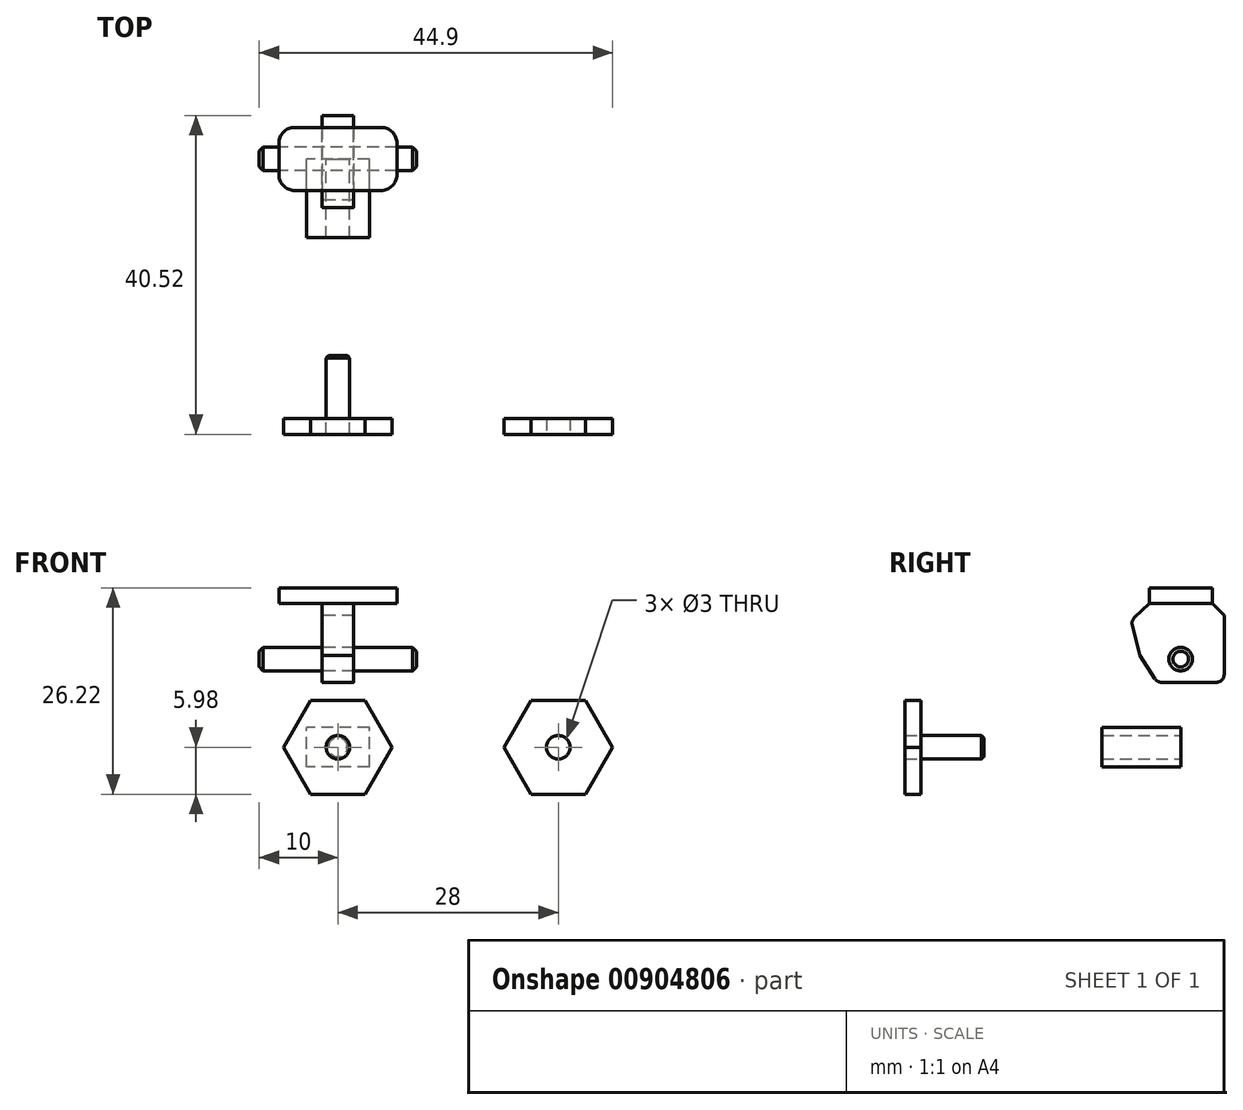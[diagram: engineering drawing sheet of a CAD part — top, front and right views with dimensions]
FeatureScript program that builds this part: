
annotation { "Feature Type Name" : "Feature", "Feature Type Description" : "" }
export const myFeature = defineFeature(function(context is Context, id is Id, definition is map)
    precondition{}
    {
        {
            var Q0;
            Q0=qCreatedBy(makeId("Front.planeOp"),FACE);
            var sketch = newSketch(context, id + "F0", { "sketchPlane" : qUnion([Q0])});
            skCircle(sketch, "E0", {"center": v(0, 0) * mm, "radius": 1.5 * mm});
            skLineSegment(sketch, "E1.bottom", {"start": v(4, -2.5) * mm, "end": v(-4, -2.5) * mm});
            skLineSegment(sketch, "E1.top", {"start": v(4, 2.5) * mm, "end": v(-4, 2.5) * mm});
            skLineSegment(sketch, "E1.left", {"start": v(4, -2.5) * mm, "end": v(4, 2.5) * mm});
            skLineSegment(sketch, "E1.right", {"start": v(-4, -2.5) * mm, "end": v(-4, 2.5) * mm});
            skSolve(sketch);
        }
        {
            var Q0;
            Q0 = qSketchRegion(id + "F0", true);
            extrude(context, id + "F1", {"entities" : qUnion([Q0]), "depth" : 10 * mm, "offsetDistance" : 25 * mm});
        }
        {
            var Q0;
            Q0=qCreatedBy(makeId("Front.planeOp"),FACE);
            cPlane(context, id + "F2", {"entities" : qUnion([Q0]), "cplaneType" : CPlaneType.OFFSET, "offset" : 25 * mm, "width" : 150 * mm, "height" : 150 * mm});
        }
        {
            var Q0;
            Q0=qCreatedBy(id+"F2.planeOp",FACE);
            var sketch = newSketch(context, id + "F3", { "sketchPlane" : qUnion([Q0])});
            skCircle(sketch, "E2", {"center": v(0, 0) * mm, "radius": 1.5 * mm});
            skSolve(sketch);
        }
        {
            var Q0;
            Q0 = qSketchRegion(id + "F3", true);
            extrude(context, id + "F4", {"entities" : qUnion([Q0]), "depth" : 10 * mm, "offsetDistance" : 25 * mm});
        }
        {
            var Q0;
            Q0=makeQuery(id+"F4.opExtrude","CAP_FACE",FACE,{"disambiguationData":[OSD([sQuery(id+"F3.wireOp",EDGE,"E2")])],"isStart":false});
            var sketch = newSketch(context, id + "F5", { "sketchPlane" : qUnion([Q0])});
            skLineSegment(sketch, "E3.0", {"start": v(6.9, 0) * mm, "end": v(3.45, -5.98) * mm});
            skLineSegment(sketch, "E3.1", {"start": v(3.45, -5.98) * mm, "end": v(-3.45, -5.98) * mm});
            skLineSegment(sketch, "E3.2", {"start": v(-3.45, -5.98) * mm, "end": v(-6.9, 0) * mm});
            skLineSegment(sketch, "E3.3", {"start": v(-6.9, 0) * mm, "end": v(-3.45, 5.98) * mm});
            skLineSegment(sketch, "E3.4", {"start": v(-3.45, 5.98) * mm, "end": v(3.45, 5.98) * mm});
            skLineSegment(sketch, "E3.5", {"start": v(3.45, 5.98) * mm, "end": v(6.9, 0) * mm});
            skPoint(sketch, "E3.0.midPoint", {"position": v(5.17, -2.99) * mm});
            skSolve(sketch);
        }
        {
            var Q0;
            Q0=makeQuery(id+"F5.imprint","IMPRINT",FACE,{"disambiguationData":[TD([[makeQuery(id+"F5.imprint","IMPRINT",EDGE,{"derivedFrom":sQuery(id+"F5.wireOp",EDGE,"E3.0")}),-1.0]])]});
            extrude(context, id + "F6", {"entities" : qUnion([Q0]), "oppositeDirection" : true, "depth" : 2 * mm, "offsetDistance" : 25 * mm});
        }
        {
            var Q0;
            Q0=makeQuery(id+"F4.opExtrude","CAP_EDGE",EDGE,{"disambiguationData":[OSD([sQuery(id+"F3.wireOp",EDGE,"E2")])],"isStart":true});
            var Q1;
            Q1=makeQuery(id+"F8.opPattern","COPY",EDGE,{"derivedFrom":makeQuery(id+"F4.opExtrude","CAP_EDGE",EDGE,{"disambiguationData":[OSD([sQuery(id+"F3.wireOp",EDGE,"E2")])],"isStart":true}),"instanceName":"1"});
            chamfer(context, id + "F7", {"entities" : qUnion([Q0, Q1]), "width" : 0.3 * mm, "tangentPropagation" : true});
        }
        {
            var Q0;
            Q0=makeQuery(id+"F6.opExtrude","SWEPT_BODY",BODY,{"disambiguationData":[OSD([sQuery(id+"F3.wireOp",EDGE,"E2"),sQuery(id+"F5.wireOp",EDGE,"E3.0"),sQuery(id+"F5.wireOp",EDGE,"E3.1"),sQuery(id+"F5.wireOp",EDGE,"E3.2"),sQuery(id+"F5.wireOp",EDGE,"E3.3"),sQuery(id+"F5.wireOp",EDGE,"E3.4"),sQuery(id+"F5.wireOp",EDGE,"E3.5")])]});
            transform(context, id + "F8", {"entities" : qUnion([Q0]), "transformType" : TransformType.TRANSLATION_3D, "dx" : 28 * mm, "dy" : 0 * mm, "dz" : 0 * mm, "makeCopy" : true});
        }
        {
            var Q0;
            Q0=qCreatedBy(makeId("Front.planeOp"),FACE);
            var sketch = newSketch(context, id + "F9", { "sketchPlane" : qUnion([Q0])});
            skLineSegment(sketch, "E4", {"start": v(0, 4.5) * mm, "end": v(0, 26.48) * mm, "construction": true});
            skLineSegment(sketch, "E5.bottom", {"start": v(7.5, 18.25) * mm, "end": v(-7.5, 18.25) * mm});
            skLineSegment(sketch, "E5.top", {"start": v(7.5, 20.24) * mm, "end": v(-7.5, 20.24) * mm});
            skLineSegment(sketch, "E5.left", {"start": v(7.5, 18.25) * mm, "end": v(7.5, 20.24) * mm});
            skLineSegment(sketch, "E5.right", {"start": v(-7.5, 18.25) * mm, "end": v(-7.5, 20.24) * mm});
            skPoint(sketch, "E5.middle", {"position": v(0, 19.25) * mm});
            skSolve(sketch);
        }
        {
            var Q0;
            Q0=makeQuery(id+"F9.imprint","IMPRINT",FACE,{"disambiguationData":[TD([[makeQuery(id+"F9.imprint","IMPRINT",EDGE,{"derivedFrom":sQuery(id+"F9.wireOp",EDGE,"E5.bottom")}),-1.0]])]});
            extrude(context, id + "F10", {"entities" : qUnion([Q0]), "endBound" : BoundingType.SYMMETRIC, "depth" : 8 * mm, "offsetDistance" : 25 * mm});
        }
        {
            var Q0;
            Q0=qCreatedBy(makeId("Right.planeOp"),FACE);
            var sketch = newSketch(context, id + "F11", { "sketchPlane" : qUnion([Q0])});
            skCircle(sketch, "E6", {"center": v(0, 11.2) * mm, "radius": 1.5 * mm});
            skSolve(sketch);
        }
        {
            var Q0;
            Q0=makeQuery(id+"F11.imprint","IMPRINT",FACE,{"disambiguationData":[TD([[makeQuery(id+"F11.imprint","IMPRINT",EDGE,{"derivedFrom":sQuery(id+"F11.wireOp",EDGE,"E6")}),1.0]])]});
            var Q1;
            Q1=sQuery(id+"F11.wireOp",EDGE,"E6");
            extrude(context, id + "F12", {"entities" : qUnion([Q0]), "surfaceEntities" : qUnion([Q1]), "endBound" : BoundingType.SYMMETRIC, "depth" : 20 * mm, "offsetDistance" : 25 * mm});
        }
        {
            var Q0;
            Q0=makeQuery(id+"F12.opExtrude","CAP_EDGE",EDGE,{"disambiguationData":[OSD([sQuery(id+"F11.wireOp",EDGE,"E6")])],"isStart":true});
            var Q1;
            Q1=makeQuery(id+"F12.opExtrude","CAP_EDGE",EDGE,{"disambiguationData":[OSD([sQuery(id+"F11.wireOp",EDGE,"E6")])],"isStart":false});
            chamfer(context, id + "F13", {"entities" : qUnion([Q0, Q1]), "width" : .5 * mm, "tangentPropagation" : true});
        }
        {
            var Q0;
            Q0=qCreatedBy(makeId("Right.planeOp"),FACE);
            var sketch = newSketch(context, id + "F14", { "sketchPlane" : qUnion([Q0])});
            skLineSegment(sketch, "E7", {"start": v(-4, 18.25) * mm, "end": v(-5.87, 16.46) * mm});
            skLineSegment(sketch, "E8", {"start": v(-6.15, 15.5) * mm, "end": v(-5.2, 11.65) * mm});
            skLineSegment(sketch, "E9", {"start": v(-5.2, 11.65) * mm, "end": v(-3.28, 8.7) * mm});
            skLineSegment(sketch, "E10", {"start": v(-2.44, 8.25) * mm, "end": v(4.52, 8.25) * mm});
            skLineSegment(sketch, "E11", {"start": v(5.52, 9.25) * mm, "end": v(5.52, 16.75) * mm});
            skLineSegment(sketch, "E12", {"start": v(5.52, 16.75) * mm, "end": v(4, 18.25) * mm});
            skLineSegment(sketch, "E13", {"start": v(4, 18.25) * mm, "end": v(-4, 18.25) * mm});
            skPoint(sketch, "E14.visualSharp", {"position": v(5.52, 8.25) * mm});
            skArc(sketch, "E14.filletArc", {"start": v(4.52, 8.25) * mm, "mid": v(5.23, 8.54) * mm, "end": v(5.52, 9.25) * mm});
            skPoint(sketch, "E15.visualSharp", {"position": v(-6.3, 16.06) * mm});
            skArc(sketch, "E15.filletArc", {"start": v(-5.87, 16.46) * mm, "mid": v(-6.14, 16.02) * mm, "end": v(-6.15, 15.5) * mm});
            skPoint(sketch, "E16.visualSharp", {"position": v(-2.98, 8.25) * mm});
            skArc(sketch, "E16.filletArc", {"start": v(-3.28, 8.7) * mm, "mid": v(-2.92, 8.37) * mm, "end": v(-2.44, 8.25) * mm});
            skLineSegment(sketch, "E17", {"start": v(4, 18.25) * mm, "end": v(4, 8.25) * mm, "construction": true});
            skSolve(sketch);
        }
        {
            var Q0;
            Q0=makeQuery(id+"F14.imprint","IMPRINT",FACE,{"disambiguationData":[TD([[makeQuery(id+"F14.imprint","IMPRINT",EDGE,{"derivedFrom":sQuery(id+"F14.wireOp",EDGE,"E7")}),1.0]])]});
            extrude(context, id + "F15", {"entities" : qUnion([Q0]), "endBound" : BoundingType.SYMMETRIC, "depth" : 4 * mm, "offsetDistance" : 25 * mm});
        }
        {
            var Q0;
            Q0=makeQuery(id+"F10.opExtrude","CAP_EDGE",EDGE,{"disambiguationData":[OSD([sQuery(id+"F9.wireOp",EDGE,"E5.left")])],"isStart":false});
            var Q1;
            Q1=makeQuery(id+"F10.opExtrude","CAP_EDGE",EDGE,{"disambiguationData":[OSD([sQuery(id+"F9.wireOp",EDGE,"E5.right")])],"isStart":false});
            var Q2;
            Q2=makeQuery(id+"F10.opExtrude","CAP_EDGE",EDGE,{"disambiguationData":[OSD([sQuery(id+"F9.wireOp",EDGE,"E5.left")])],"isStart":true});
            var Q3;
            Q3=makeQuery(id+"F10.opExtrude","CAP_EDGE",EDGE,{"disambiguationData":[OSD([sQuery(id+"F9.wireOp",EDGE,"E5.right")])],"isStart":true});
            fillet(context, id + "F16", {"entities" : qUnion([Q0, Q1, Q2, Q3]), "radius" : 2 * mm, "tangentPropagation" : true, "allowEdgeOverflow" : false});
        }
    });
